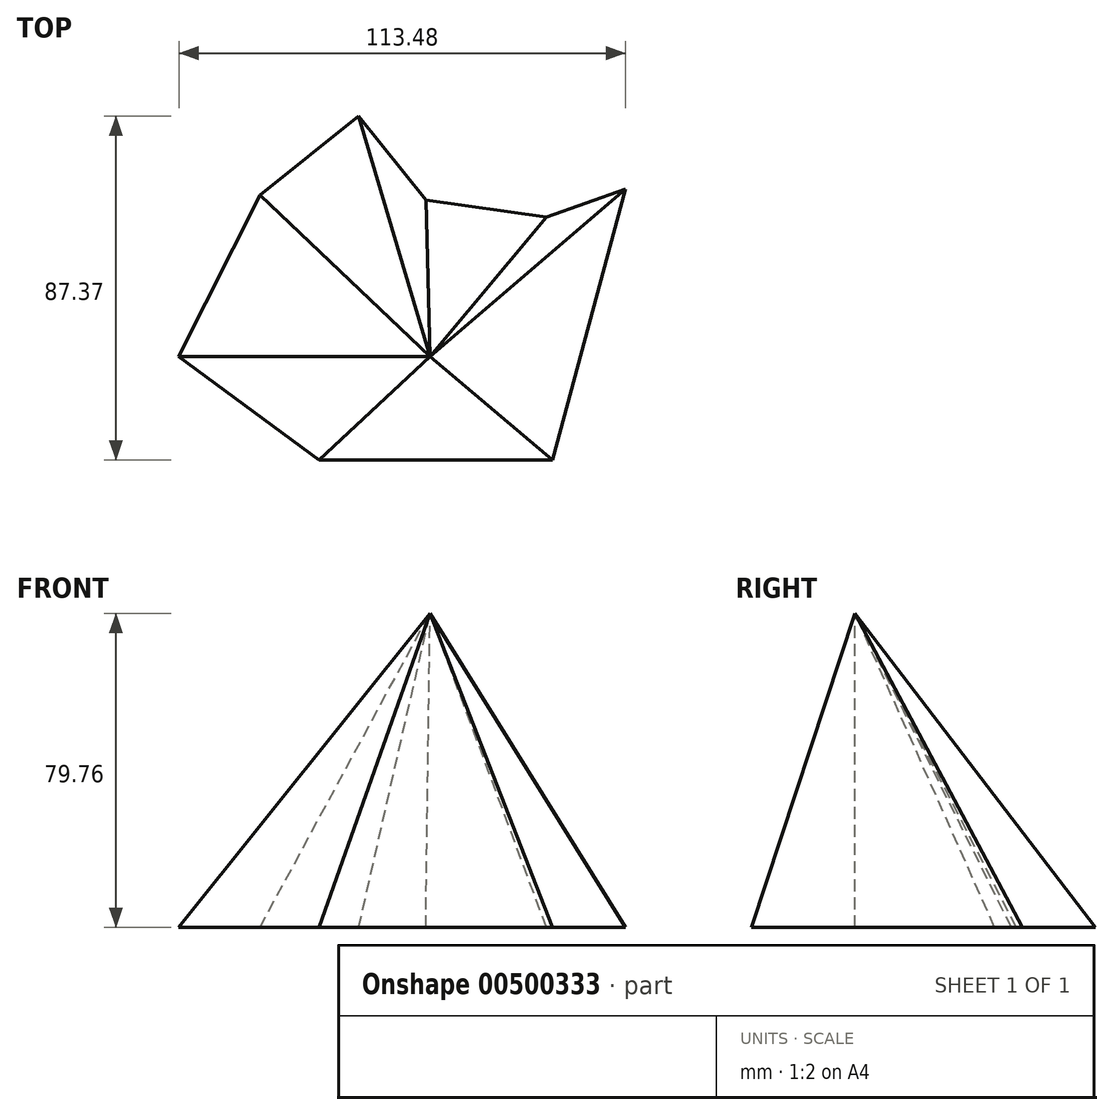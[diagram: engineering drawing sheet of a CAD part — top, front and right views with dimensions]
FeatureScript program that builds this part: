
annotation { "Feature Type Name" : "Feature", "Feature Type Description" : "" }
export const myFeature = defineFeature(function(context is Context, id is Id, definition is map)
    precondition{}
    {
        {
            var Q0;
            Q0=qCreatedBy(makeId("Top.planeOp"),FACE);
            var sketch = newSketch(context, id + "F0", { "sketchPlane" : qUnion([Q0])});
            skLineSegment(sketch, "E0", {"start": v(-49.02, 40.95) * mm, "end": v(-23.9, 61.03) * mm});
            skLineSegment(sketch, "E1", {"start": v(-23.9, 61.03) * mm, "end": v(-6.86, 39.72) * mm});
            skLineSegment(sketch, "E2", {"start": v(-6.86, 39.72) * mm, "end": v(23.8, 35.43) * mm});
            skLineSegment(sketch, "E3", {"start": v(23.8, 35.43) * mm, "end": v(43.88, 42.46) * mm});
            skLineSegment(sketch, "E4", {"start": v(43.88, 42.46) * mm, "end": v(25.3, -26.34) * mm});
            skLineSegment(sketch, "E5", {"start": v(25.3, -26.34) * mm, "end": v(-33.95, -26.34) * mm});
            skLineSegment(sketch, "E6", {"start": v(-33.95, -26.34) * mm, "end": v(-69.6, 0) * mm});
            skLineSegment(sketch, "E7", {"start": v(-69.6, 0) * mm, "end": v(-49.02, 40.95) * mm});
            skSolve(sketch);
        }
        {
            var Q0;
            Q0=qCreatedBy(makeId("Top.planeOp"),FACE);
            cPlane(context, id + "F1", {"entities" : qUnion([Q0]), "cplaneType" : CPlaneType.OFFSET, "offset" : 79.76 * mm, "width" : 152.4 * mm, "height" : 152.4 * mm});
        }
        {
            var Q0;
            Q0=qCreatedBy(id+"F1.planeOp",FACE);
            var sketch = newSketch(context, id + "F2", { "sketchPlane" : qUnion([Q0])});
            skPoint(sketch, "E8", {"position": v(-5.8, 0) * mm});
            skSolve(sketch);
        }
        {
            var Q0;
            Q0=makeQuery(id+"F0.imprint","IMPRINT",FACE,{"disambiguationData":[TD([[makeQuery(id+"F0.imprint","IMPRINT",EDGE,{"derivedFrom":sQuery(id+"F0.wireOp",EDGE,"E0")}),-1.0]])]});
            var Q1;
            Q1=sQuery(id+"F2.wireOp",VERTEX,"E8");
            loft(context, id + "F3", {"sheetProfilesArray" : [{ "sheetProfileEntities" : qUnion([Q0]) }, { "sheetProfileEntities" : qUnion([Q1]) }]});
        }
    });
